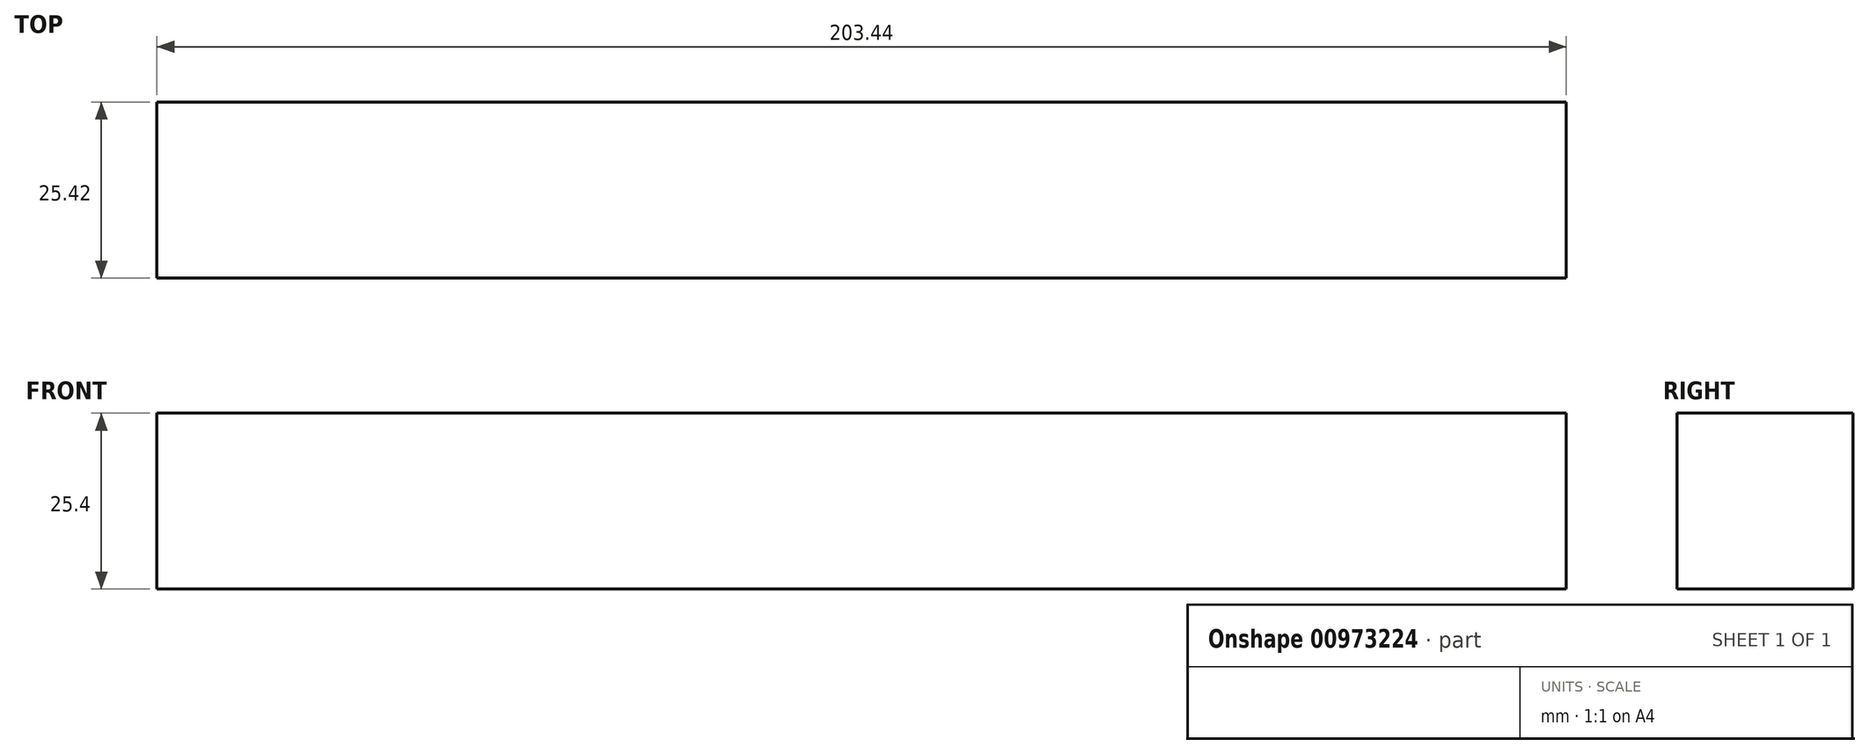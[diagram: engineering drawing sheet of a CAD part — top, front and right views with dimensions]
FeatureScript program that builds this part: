
annotation { "Feature Type Name" : "Feature", "Feature Type Description" : "" }
export const myFeature = defineFeature(function(context is Context, id is Id, definition is map)
    precondition{}
    {
        {
            var Q0;
            Q0=qCreatedBy(makeId("Top.planeOp"),FACE);
            var sketch = newSketch(context, id + "F0", { "sketchPlane" : qUnion([Q0])});
            skLineSegment(sketch, "E0.bottom", {"start": v(-101.72, -12.71) * mm, "end": v(101.72, -12.71) * mm});
            skLineSegment(sketch, "E0.top", {"start": v(-101.72, 12.71) * mm, "end": v(101.72, 12.71) * mm});
            skLineSegment(sketch, "E0.left", {"start": v(-101.72, -12.71) * mm, "end": v(-101.72, 12.71) * mm});
            skLineSegment(sketch, "E0.right", {"start": v(101.72, -12.71) * mm, "end": v(101.72, 12.71) * mm});
            skPoint(sketch, "E0.middle", {"position": v(0, 0) * mm});
            skSolve(sketch);
        }
        {
            var Q0;
            Q0 = qSketchRegion(id + "F0", true);
            extrude(context, id + "F1", {"entities" : qUnion([Q0]), "depth" : 25.4 * mm, "offsetDistance" : 25.4 * mm});
        }
    });
